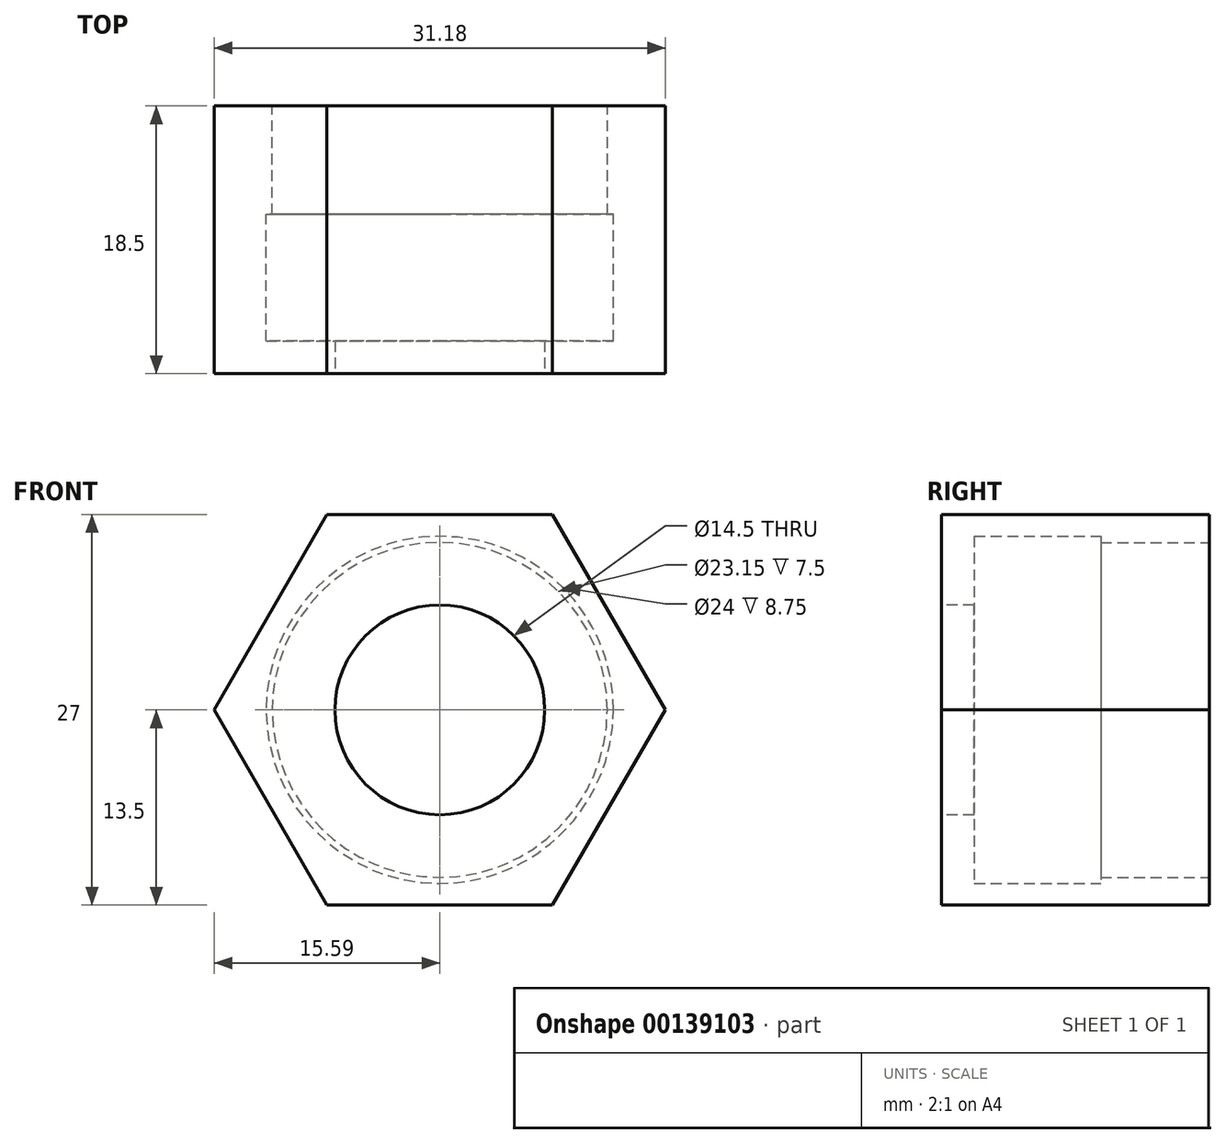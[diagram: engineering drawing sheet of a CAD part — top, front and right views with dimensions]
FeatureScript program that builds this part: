
annotation { "Feature Type Name" : "Feature", "Feature Type Description" : "" }
export const myFeature = defineFeature(function(context is Context, id is Id, definition is map)
    precondition{}
    {
        {
            var Q0;
            Q0=qCreatedBy(makeId("Front.planeOp"),FACE);
            var sketch = newSketch(context, id + "F0", { "sketchPlane" : qUnion([Q0])});
            skCircle(sketch, "E0.cCircle", {"center": v(0, 0) * mm, "radius": 13.5 * mm, "construction": true});
            skLineSegment(sketch, "E0.0", {"start": v(-7.8, 13.5) * mm, "end": v(7.8, 13.5) * mm});
            skLineSegment(sketch, "E0.1", {"start": v(7.8, 13.5) * mm, "end": v(15.59, 0) * mm});
            skLineSegment(sketch, "E0.2", {"start": v(15.59, 0) * mm, "end": v(7.8, -13.5) * mm});
            skLineSegment(sketch, "E0.3", {"start": v(7.8, -13.5) * mm, "end": v(-7.8, -13.5) * mm});
            skLineSegment(sketch, "E0.4", {"start": v(-7.8, -13.5) * mm, "end": v(-15.59, 0) * mm});
            skLineSegment(sketch, "E0.5", {"start": v(-15.59, 0) * mm, "end": v(-7.8, 13.5) * mm});
            skPoint(sketch, "E0.0.midPoint", {"position": v(0, 13.5) * mm});
            skSolve(sketch);
        }
        {
            var Q0;
            Q0 = qSketchRegion(id + "F0", true);
            extrude(context, id + "F1", {"entities" : qUnion([Q0]), "depth" : 18.5 * mm});
        }
        {
            var Q0;
            Q0=makeQuery(id+"F1.opExtrude","CAP_FACE",FACE,{"disambiguationData":[OSD([sQuery(id+"F0.wireOp",EDGE,"E0.0"),sQuery(id+"F0.wireOp",EDGE,"E0.1"),sQuery(id+"F0.wireOp",EDGE,"E0.2"),sQuery(id+"F0.wireOp",EDGE,"E0.3"),sQuery(id+"F0.wireOp",EDGE,"E0.4"),sQuery(id+"F0.wireOp",EDGE,"E0.5")])],"isStart":false});
            var sketch = newSketch(context, id + "F2", { "sketchPlane" : qUnion([Q0])});
            skCircle(sketch, "E1", {"center": v(0, 0) * mm, "radius": 7.25 * mm});
            skSolve(sketch);
        }
        {
            var Q0;
            Q0 = qSketchRegion(id + "F2", true);
            extrude(context, id + "F3", {"entities" : qUnion([Q0]), "operationType" : NewBodyOperationType.REMOVE, "endBound" : BoundingType.THROUGH_ALL, "oppositeDirection" : true, "depth" : 25 * mm});
        }
        {
            var Q0;
            Q0=qCreatedBy(makeId("Right.planeOp"),FACE);
            var sketch = newSketch(context, id + "F4", { "sketchPlane" : qUnion([Q0])});
            skLineSegment(sketch, "E2", {"start": v(0, 0) * mm, "end": v(0, 11.58) * mm});
            skLineSegment(sketch, "E3", {"start": v(0, 11.58) * mm, "end": v(-7.5, 11.58) * mm});
            skLineSegment(sketch, "E4", {"start": v(-7.5, 11.58) * mm, "end": v(-7.5, 12) * mm});
            skLineSegment(sketch, "E5", {"start": v(-7.5, 12) * mm, "end": v(-16.25, 12) * mm});
            skLineSegment(sketch, "E6", {"start": v(-16.25, 12) * mm, "end": v(-16.25, 0) * mm});
            skLineSegment(sketch, "E7", {"start": v(-16.25, 0) * mm, "end": v(0, 0) * mm});
            skSolve(sketch);
        }
        {
            var Q0;
            Q0 = qSketchRegion(id + "F4", true);
            var Q1;
            Q1=sQuery(id+"F4.wireOp",EDGE,"E7");
            revolve(context, id + "F5", {"operationType" : NewBodyOperationType.REMOVE, "entities" : qUnion([Q0]), "axis" : qUnion([Q1]), "revolveType" : RevolveType.FULL, "oppositeDirection" : true});
        }
    });
